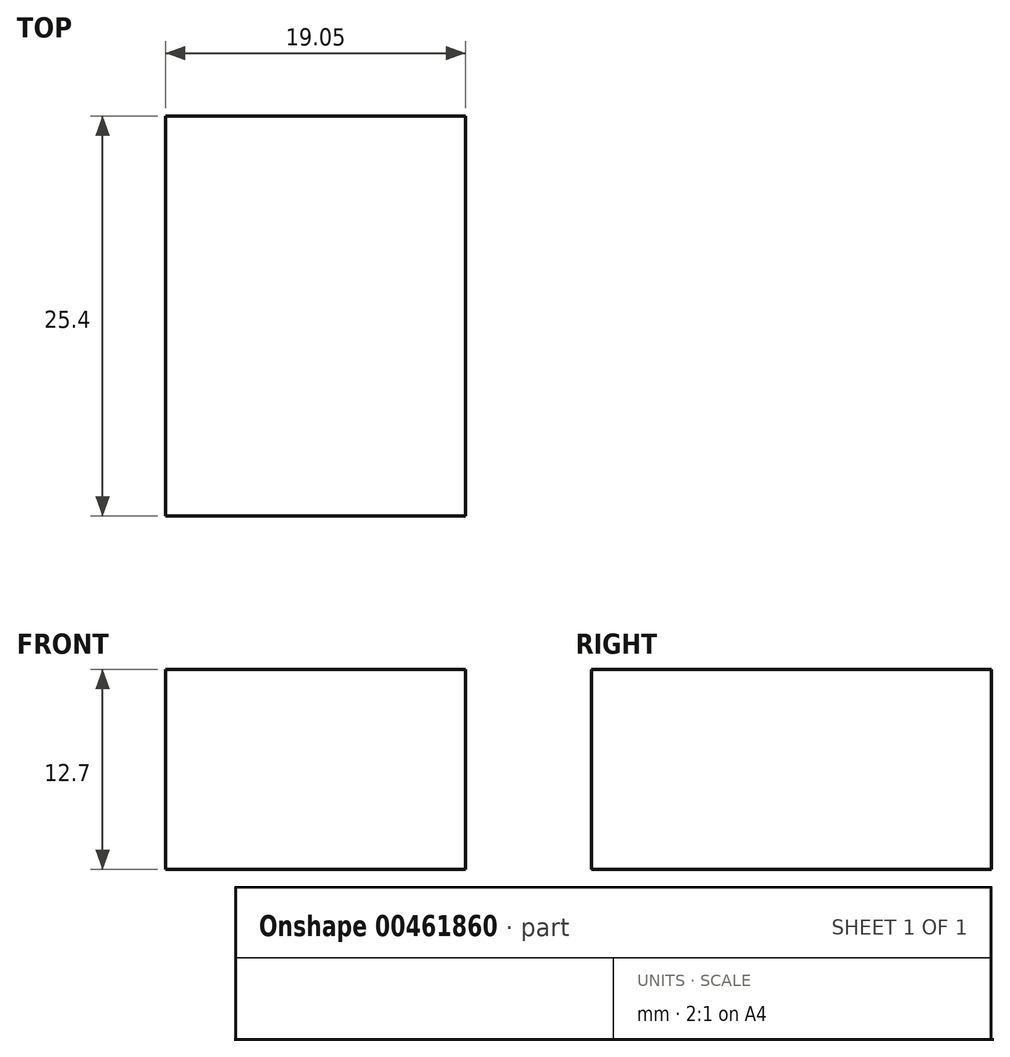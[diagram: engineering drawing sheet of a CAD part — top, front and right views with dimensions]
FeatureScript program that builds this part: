
annotation { "Feature Type Name" : "Feature", "Feature Type Description" : "" }
export const myFeature = defineFeature(function(context is Context, id is Id, definition is map)
    precondition{}
    {
        {
            var Q0;
            Q0=qCreatedBy(makeId("Front.planeOp"),FACE);
            var sketch = newSketch(context, id + "F0", { "sketchPlane" : qUnion([Q0])});
            skLineSegment(sketch, "E0.bottom", {"start": v(-50.8, 25.4) * mm, "end": v(50.8, 25.4) * mm});
            skLineSegment(sketch, "E0.top", {"start": v(-50.8, -25.4) * mm, "end": v(50.8, -25.4) * mm});
            skLineSegment(sketch, "E0.left", {"start": v(-50.8, 25.4) * mm, "end": v(-50.8, -25.4) * mm});
            skLineSegment(sketch, "E0.right", {"start": v(50.8, 25.4) * mm, "end": v(50.8, -25.4) * mm});
            skPoint(sketch, "E0.middle", {"position": v(0, 0) * mm});
            skLineSegment(sketch, "E1.bottom", {"start": v(-25.4, 25.4) * mm, "end": v(25.4, 25.4) * mm});
            skLineSegment(sketch, "E1.top", {"start": v(-25.4, 12.7) * mm, "end": v(25.4, 12.7) * mm});
            skLineSegment(sketch, "E1.left", {"start": v(-25.4, 25.4) * mm, "end": v(-25.4, 12.7) * mm});
            skLineSegment(sketch, "E1.right", {"start": v(25.4, 25.4) * mm, "end": v(25.4, 12.7) * mm});
            skLineSegment(sketch, "E2.bottom", {"start": v(50.8, -12.7) * mm, "end": v(31.75, -12.7) * mm});
            skLineSegment(sketch, "E2.top", {"start": v(50.8, -25.4) * mm, "end": v(31.75, -25.4) * mm});
            skLineSegment(sketch, "E2.left", {"start": v(50.8, -12.7) * mm, "end": v(50.8, -25.4) * mm});
            skLineSegment(sketch, "E2.right", {"start": v(31.75, -12.7) * mm, "end": v(31.75, -25.4) * mm});
            skSolve(sketch);
        }
        {
            var Q0;
            Q0=makeQuery(id+"F0.imprint","IMPRINT",FACE,{"disambiguationData":[TD([[makeQuery(id+"F0.imprint","IMPRINT",EDGE,{"derivedFrom":sQuery(id+"F0.wireOp",EDGE,"E0.top")}),1.0]])]});
            extrude(context, id + "F1", {"entities" : qUnion([Q0]), "depth" : 25.4 * mm});
        }
        {
            var Q0;
            Q0=makeQuery(id+"F1.opExtrude","SWEPT_FACE",FACE,{"disambiguationData":[OSD([sQuery(id+"F0.wireOp",EDGE,"E0.right")])]});
            var sketch = newSketch(context, id + "F2", { "sketchPlane" : qUnion([Q0])});
            skCircle(sketch, "E3", {"center": v(-12.7, 0) * mm, "radius": 5.82 * mm});
            skSolve(sketch);
        }
        {
            var Q0;
            Q0=makeQuery(id+"F2.imprint","IMPRINT",FACE,{"disambiguationData":[TD([[makeQuery(id+"F2.imprint","IMPRINT",EDGE,{"derivedFrom":sQuery(id+"F2.wireOp",EDGE,"E3")}),1.0]])]});
            extrude(context, id + "F3", {"entities" : qUnion([Q0]), "operationType" : NewBodyOperationType.REMOVE, "endBound" : BoundingType.THROUGH_ALL, "oppositeDirection" : true, "depth" : 25.4 * mm});
        }
    });
